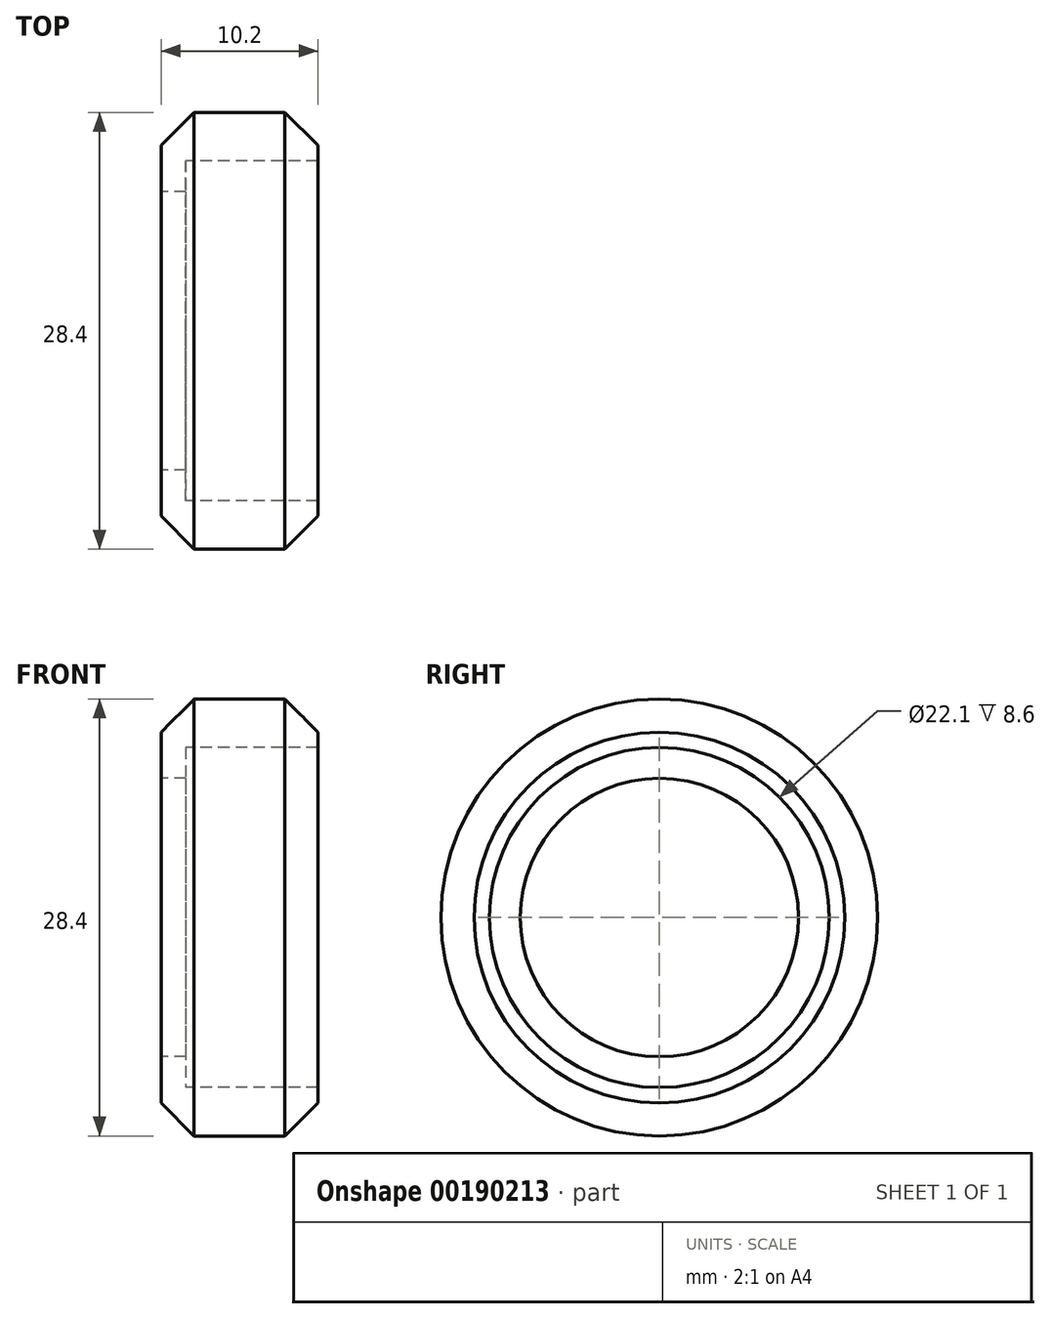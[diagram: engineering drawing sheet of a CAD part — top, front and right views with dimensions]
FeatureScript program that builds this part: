
annotation { "Feature Type Name" : "Feature", "Feature Type Description" : "" }
export const myFeature = defineFeature(function(context is Context, id is Id, definition is map)
    precondition{}
    {
        {
            var Q0;
            Q0=qCreatedBy(makeId("Front.planeOp"),FACE);
            var sketch = newSketch(context, id + "F0", { "sketchPlane" : qUnion([Q0])});
            skLineSegment(sketch, "E0", {"start": v(0, 0) * mm, "end": v(7.5, 0) * mm, "construction": true});
            skLineSegment(sketch, "E1", {"start": v(-5.1, 11.05) * mm, "end": v(5.1, 11.05) * mm});
            skLineSegment(sketch, "E2", {"start": v(5.1, 11.05) * mm, "end": v(5.1, 12.05) * mm});
            skLineSegment(sketch, "E3", {"start": v(5.1, 12.05) * mm, "end": v(2.95, 14.2) * mm});
            skLineSegment(sketch, "E4", {"start": v(2.95, 14.2) * mm, "end": v(-2.95, 14.2) * mm});
            skLineSegment(sketch, "E5", {"start": v(-2.95, 14.2) * mm, "end": v(-5.1, 12.05) * mm});
            skLineSegment(sketch, "E6", {"start": v(-5.1, 12.05) * mm, "end": v(-5.1, 11.05) * mm});
            skLineSegment(sketch, "E7", {"start": v(0, 0) * mm, "end": v(0, 11.05) * mm, "construction": true});
            skLineSegment(sketch, "E8", {"start": v(0, 11.05) * mm, "end": v(0, 14.2) * mm, "construction": true});
            skLineSegment(sketch, "E9", {"start": v(-5.1, 11.05) * mm, "end": v(-5.1, 9.05) * mm});
            skLineSegment(sketch, "E10", {"start": v(-5.1, 9.05) * mm, "end": v(-3.5, 9.05) * mm});
            skLineSegment(sketch, "E11", {"start": v(-3.5, 9.05) * mm, "end": v(-3.5, 11.05) * mm});
            skPoint(sketch, "E12", {"position": v(-5.1, 12.05) * mm});
            skLineSegment(sketch, "E13", {"start": v(3.4, 11.05) * mm, "end": v(3.45, 11) * mm, "construction": true});
            skLineSegment(sketch, "E14", {"start": v(3.45, 11) * mm, "end": v(3.5, 11.05) * mm, "construction": true});
            skLineSegment(sketch, "E15", {"start": v(3.45, 11) * mm, "end": v(3.95, 11) * mm, "construction": true});
            skLineSegment(sketch, "E16", {"start": v(3.95, 11) * mm, "end": v(4, 11.05) * mm, "construction": true});
            skSolve(sketch);
        }
        {
            var Q0;
            {var subQ0=sQuery(id+"F0.wireOp",EDGE,"E2");Q0=makeQuery(id+"F0.imprint","IMPRINT",FACE,{"disambiguationData":[TD([[makeQuery(id+"F0.imprint","IMPRINT",EDGE,{"derivedFrom":subQ0}),1.0]])]});}
            var Q1;
            {var subQ0=sQuery(id+"F0.wireOp",EDGE,"E9");Q1=makeQuery(id+"F0.imprint","IMPRINT",FACE,{"disambiguationData":[TD([[makeQuery(id+"F0.imprint","IMPRINT",EDGE,{"derivedFrom":subQ0}),1.0]])]});}
            var Q2;
            {var subQ0=sQuery(id+"F0.wireOp",EDGE,"E13");Q2=makeQuery(id+"F0.imprint","IMPRINT",FACE,{"disambiguationData":[TD([[makeQuery(id+"F0.imprint","IMPRINT",EDGE,{"derivedFrom":subQ0}),1.0]])]});}
            var Q3;
            Q3=sQuery(id+"F0.wireOp",EDGE,"E0");
            revolve(context, id + "F1", {"entities" : qUnion([Q0, Q1, Q2]), "axis" : qUnion([Q3]), "revolveType" : RevolveType.FULL});
        }
    });
